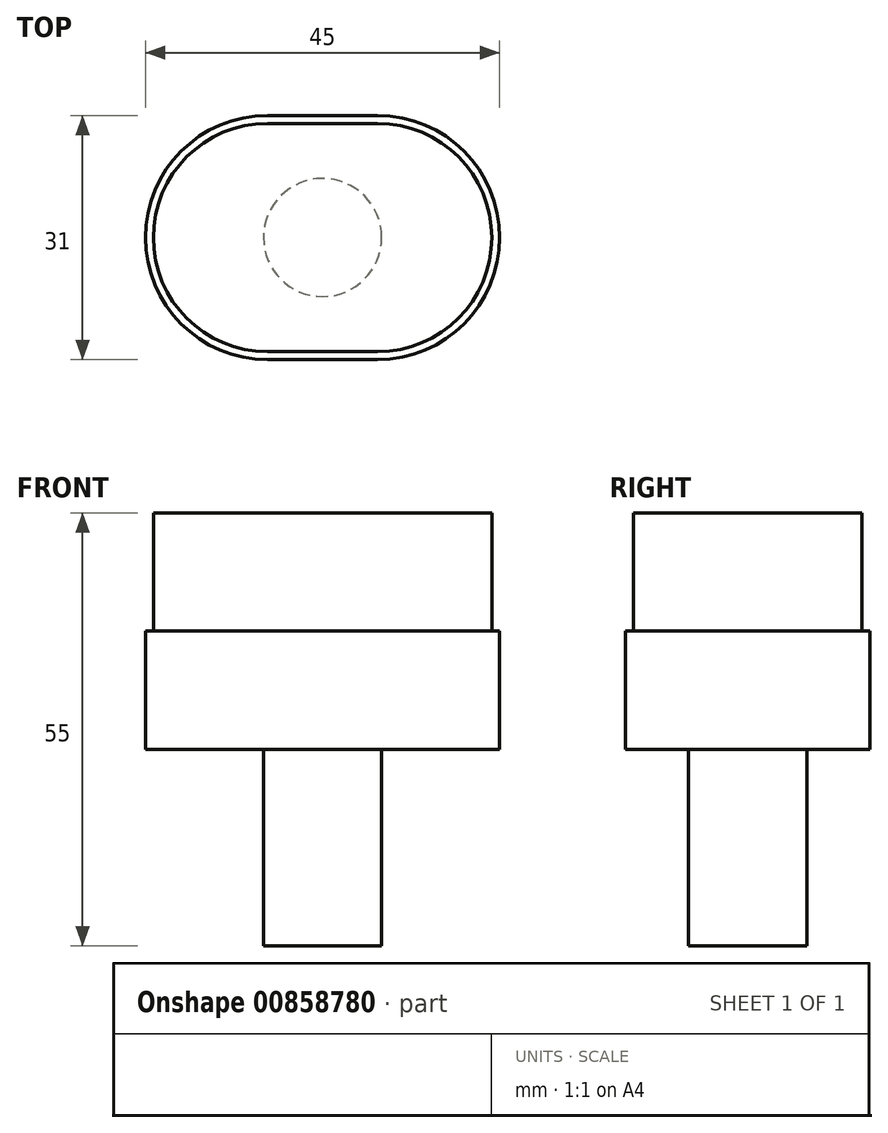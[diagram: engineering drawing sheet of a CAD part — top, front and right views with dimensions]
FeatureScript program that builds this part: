
annotation { "Feature Type Name" : "Feature", "Feature Type Description" : "" }
export const myFeature = defineFeature(function(context is Context, id is Id, definition is map)
    precondition{}
    {
        {
            var Q0;
            Q0=qCreatedBy(makeId("Top.planeOp"),FACE);
            var sketch = newSketch(context, id + "F0", { "sketchPlane" : qUnion([Q0])});
            skLineSegment(sketch, "E0.bottom", {"start": v(7, 15.5) * mm, "end": v(-7, 15.5) * mm});
            skLineSegment(sketch, "E0.top", {"start": v(7, -15.5) * mm, "end": v(-7, -15.5) * mm});
            skPoint(sketch, "E0.middle", {"position": v(0, 0) * mm});
            skLineSegment(sketch, "E1", {"start": v(22.5, 0) * mm, "end": v(7, 0) * mm});
            skArc(sketch, "E2", {"start": v(7, -15.5) * mm, "mid": v(22.5, 0) * mm, "end": v(7, 15.5) * mm});
            skLineSegment(sketch, "E3", {"start": v(-22.5, 0) * mm, "end": v(-7, 0) * mm});
            skArc(sketch, "E4", {"start": v(-7, 15.5) * mm, "mid": v(-22.5, 0) * mm, "end": v(-7, -15.5) * mm});
            skPoint(sketch, "E5.orphan", {"position": v(-22.5, 15.5) * mm});
            skPoint(sketch, "E6.orphan", {"position": v(22.5, 15.5) * mm});
            skPoint(sketch, "E0.left.end.orphan", {"position": v(22.5, -15.5) * mm});
            skPoint(sketch, "E0.right.end.orphan", {"position": v(-22.5, -15.5) * mm});
            skLineSegment(sketch, "E7", {"start": v(0, 0) * mm, "end": v(-7, 0) * mm});
            skLineSegment(sketch, "E8", {"start": v(0, 0) * mm, "end": v(7, 0) * mm});
            skSolve(sketch);
        }
        {
            var Q0;
            Q0 = qSketchRegion(id + "F0", true);
            extrude(context, id + "F1", {"entities" : qUnion([Q0]), "depth" : 15 * mm, "offsetDistance" : 25 * mm});
        }
        {
            var Q0;
            Q0=makeQuery(id+"F1.opExtrude","CAP_FACE",FACE,{"disambiguationData":[OSD([sQuery(id+"F0.wireOp",EDGE,"E0.bottom"),sQuery(id+"F0.wireOp",EDGE,"E0.top"),sQuery(id+"F0.wireOp",EDGE,"E2"),sQuery(id+"F0.wireOp",EDGE,"E4")])],"isStart":false});
            var sketch = newSketch(context, id + "F2", { "sketchPlane" : qUnion([Q0])});
            skLineSegment(sketch, "E9.bottom", {"start": v(7, 14.5) * mm, "end": v(-7, 14.5) * mm});
            skLineSegment(sketch, "E9.top", {"start": v(7, -14.5) * mm, "end": v(-7, -14.5) * mm});
            skPoint(sketch, "E9.middle", {"position": v(0, 0) * mm});
            skLineSegment(sketch, "E10", {"start": v(-21.5, 0) * mm, "end": v(-7, 0) * mm});
            skLineSegment(sketch, "E11", {"start": v(-7, 0) * mm, "end": v(0, 0) * mm});
            skLineSegment(sketch, "E12", {"start": v(21.5, 0) * mm, "end": v(7, 0) * mm});
            skLineSegment(sketch, "E13", {"start": v(7, 0) * mm, "end": v(0, 0) * mm});
            skArc(sketch, "E14", {"start": v(7, 14.5) * mm, "mid": v(21.5, 0) * mm, "end": v(7, -14.5) * mm});
            skArc(sketch, "E15", {"start": v(-7, 14.5) * mm, "mid": v(-21.5, 0) * mm, "end": v(-7, -14.5) * mm});
            skPoint(sketch, "E16.orphan", {"position": v(-21.5, 14.5) * mm});
            skPoint(sketch, "E17.orphan", {"position": v(-21.5, -14.5) * mm});
            skPoint(sketch, "E18.orphan", {"position": v(21.5, -14.5) * mm});
            skPoint(sketch, "E19.orphan", {"position": v(21.5, 14.5) * mm});
            skSolve(sketch);
        }
        {
            var Q0;
            Q0 = qSketchRegion(id + "F2", true);
            extrude(context, id + "F3", {"entities" : qUnion([Q0]), "operationType" : NewBodyOperationType.ADD, "depth" : 15 * mm, "offsetDistance" : 25 * mm});
        }
        {
            var Q0;
            Q0=makeQuery(id+"F1.opExtrude","CAP_FACE",FACE,{"disambiguationData":[OSD([sQuery(id+"F0.wireOp",EDGE,"E0.bottom"),sQuery(id+"F0.wireOp",EDGE,"E0.top"),sQuery(id+"F0.wireOp",EDGE,"E2"),sQuery(id+"F0.wireOp",EDGE,"E4")])],"isStart":true});
            var sketch = newSketch(context, id + "F4", { "sketchPlane" : qUnion([Q0])});
            skCircle(sketch, "E20", {"center": v(0, 0) * mm, "radius": 7.5 * mm});
            skSolve(sketch);
        }
        {
            var Q0;
            Q0 = qSketchRegion(id + "F4", true);
            extrude(context, id + "F5", {"entities" : qUnion([Q0]), "operationType" : NewBodyOperationType.ADD, "depth" : 25 * mm, "offsetDistance" : 25 * mm});
        }
    });
